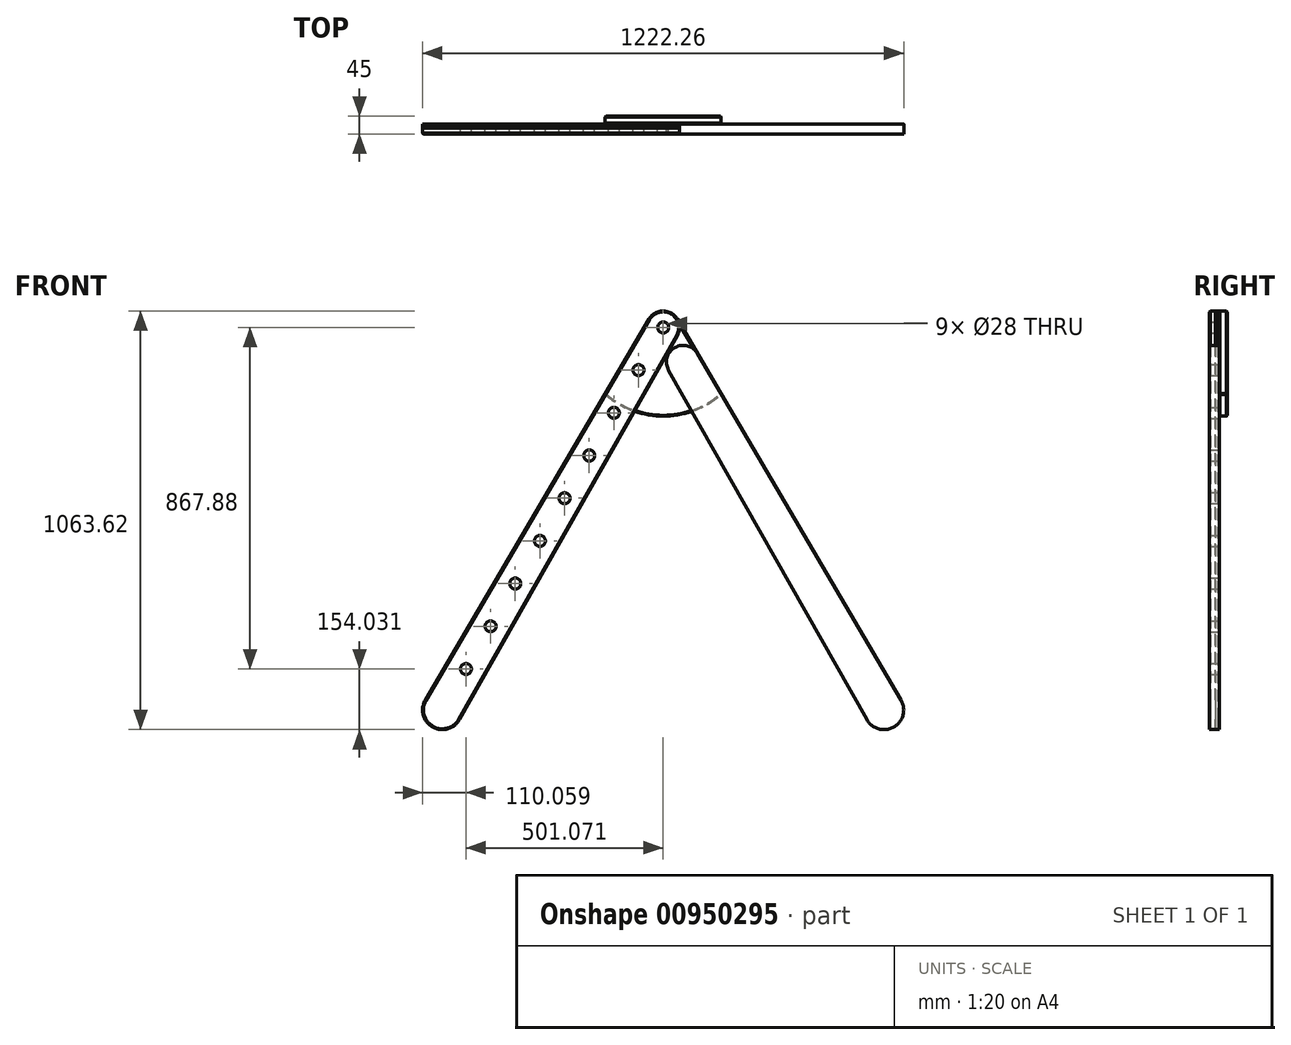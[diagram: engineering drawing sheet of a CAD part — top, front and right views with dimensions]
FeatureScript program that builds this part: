
annotation { "Feature Type Name" : "Feature", "Feature Type Description" : "" }
export const myFeature = defineFeature(function(context is Context, id is Id, definition is map)
    precondition{}
    {
        {
            var Q0;
            Q0=qCreatedBy(makeId("Front.planeOp"),FACE);
            var sketch = newSketch(context, id + "F0", { "sketchPlane" : qUnion([Q0])});
            skLineSegment(sketch, "E0", {"start": v(0, -771.5) * mm, "end": v(-590, -771.5) * mm});
            skLineSegment(sketch, "E1", {"start": v(-590, -771.5) * mm, "end": v(0, 250.4) * mm});
            skLineSegment(sketch, "E2", {"start": v(0, 250.4) * mm, "end": v(0, -771.5) * mm});
            skSolve(sketch);
        }
        {
            var Q0;
            Q0=qCreatedBy(makeId("Front.planeOp"),FACE);
            var sketch = newSketch(context, id + "F1", { "sketchPlane" : qUnion([Q0])});
            skCircle(sketch, "E3", {"center": v(-501.07, -617.48) * mm, "radius": 14 * mm});
            skCircle(sketch, "E4.1.0.0", {"center": v(-438.44, -509) * mm, "radius": 14 * mm});
            skCircle(sketch, "E4.2.0.0", {"center": v(-375.8, -400.5) * mm, "radius": 14 * mm});
            skCircle(sketch, "E4.3.0.0", {"center": v(-313.17, -292.02) * mm, "radius": 14 * mm});
            skCircle(sketch, "E4.4.0.0", {"center": v(-250.54, -183.54) * mm, "radius": 14 * mm});
            skCircle(sketch, "E4.5.0.0", {"center": v(-187.9, -75.05) * mm, "radius": 14 * mm});
            skCircle(sketch, "E4.6.0.0", {"center": v(-125.27, 33.43) * mm, "radius": 14 * mm});
            skCircle(sketch, "E4.7.0.0", {"center": v(-62.63, 141.92) * mm, "radius": 14 * mm});
            skCircle(sketch, "E4.8.0.0", {"center": v(0, 250.4) * mm, "radius": 14 * mm});
            skLineSegment(sketch, "E4.direction1", {"start": v(-501.07, -617.48) * mm, "end": v(-438.44, -509) * mm, "construction": true});
            skSolve(sketch);
        }
        {
            var Q0;
            Q0=qCreatedBy(makeId("Front.planeOp"),FACE);
            var sketch = newSketch(context, id + "F2", { "sketchPlane" : qUnion([Q0])});
            skArc(sketch, "E5", {"start": v(-604.25, -696.19) * mm, "mid": v(-586.13, -764.81) * mm, "end": v(-517.65, -746.19) * mm});
            skLineSegment(sketch, "E6", {"start": v(-604.25, -696.19) * mm, "end": v(-35.97, 271.52) * mm});
            skArc(sketch, "E7", {"start": v(36.28, 229.81) * mm, "mid": v(20.86, 286.53) * mm, "end": v(-35.97, 271.52) * mm});
            skLineSegment(sketch, "E8", {"start": v(36.28, 229.81) * mm, "end": v(-517.65, -746.19) * mm});
            skPoint(sketch, "E9.end.orphan", {"position": v(0, 304.4) * mm});
            skArc(sketch, "E10.MirrorCS", {"start": v(604.25, -696.19) * mm, "mid": v(586.13, -764.81) * mm, "end": v(517.65, -746.19) * mm});
            skLineSegment(sketch, "E11.MirrorCS", {"start": v(604.25, -696.19) * mm, "end": v(35.97, 271.52) * mm});
            skLineSegment(sketch, "E12.MirrorCS", {"start": v(0, 165.9) * mm, "end": v(517.65, -746.19) * mm});
            skLineSegment(sketch, "E13", {"start": v(0, 250.4) * mm, "end": v(561.13, -721.5) * mm});
            skPoint(sketch, "E14.orphan", {"position": v(-36.28, 229.81) * mm});
            skCircle(sketch, "E15", {"center": v(50.78, 162.45) * mm, "radius": 42.46 * mm});
            skSolve(sketch);
        }
        {
            var Q0;
            Q0=qCreatedBy(makeId("Front.planeOp"),FACE);
            var sketch = newSketch(context, id + "F3", { "sketchPlane" : qUnion([Q0])});
            skLineSegment(sketch, "E16.0", {"start": v(604.25, -696.19) * mm, "end": v(87.4, 183.95) * mm});
            skArc(sketch, "E16.1", {"start": v(87.4, 183.95) * mm, "mid": v(29.55, 199.22) * mm, "end": v(13.85, 141.49) * mm});
            skLineSegment(sketch, "E16.2", {"start": v(13.85, 141.49) * mm, "end": v(517.65, -746.19) * mm});
            skArc(sketch, "E16.3", {"start": v(604.25, -696.19) * mm, "mid": v(586.13, -764.81) * mm, "end": v(517.65, -746.19) * mm});
            skPoint(sketch, "E17.orphan", {"position": v(35.97, 271.52) * mm});
            skPoint(sketch, "E18.orphan", {"position": v(0, 165.9) * mm});
            skSolve(sketch);
        }
        {
            var Q0;
            Q0 = qSketchRegion(id + "F3", true);
            extrude(context, id + "F4", {"entities" : qUnion([Q0]), "depth" : 25 * mm, "offsetDistance" : 25 * mm});
        }
        {
            var Q0;
            Q0=qCreatedBy(makeId("Front.planeOp"),FACE);
            var sketch = newSketch(context, id + "F5", { "sketchPlane" : qUnion([Q0])});
            skArc(sketch, "E19.0", {"start": v(-604.25, -696.19) * mm, "mid": v(-586.13, -764.81) * mm, "end": v(-517.65, -746.19) * mm});
            skLineSegment(sketch, "E19.1", {"start": v(-604.25, -696.19) * mm, "end": v(-35.97, 271.52) * mm});
            skArc(sketch, "E19.2", {"start": v(36.28, 229.81) * mm, "mid": v(20.86, 286.53) * mm, "end": v(-35.97, 271.52) * mm});
            skLineSegment(sketch, "E19.3", {"start": v(36.28, 229.81) * mm, "end": v(-517.65, -746.19) * mm});
            skSolve(sketch);
        }
        {
            var Q0;
            Q0 = qSketchRegion(id + "F5", true);
            extrude(context, id + "F6", {"entities" : qUnion([Q0]), "depth" : 25 * mm, "offsetDistance" : 25 * mm});
        }
        {
            var Q0;
            Q0=qCreatedBy(makeId("Front.planeOp"),FACE);
            var sketch = newSketch(context, id + "F7", { "sketchPlane" : qUnion([Q0])});
            skArc(sketch, "E20", {"start": v(-148.1, 80.58) * mm, "mid": v(0, 25.07) * mm, "end": v(148.1, 80.58) * mm});
            skLineSegment(sketch, "E21.0", {"start": v(604.25, -696.19) * mm, "end": v(35.97, 271.52) * mm});
            skLineSegment(sketch, "E21.1", {"start": v(-604.25, -696.19) * mm, "end": v(-35.97, 271.52) * mm});
            skPoint(sketch, "E21.2", {"position": v(-35.97, 271.52) * mm});
            skArc(sketch, "E21.3", {"start": v(35.97, 271.52) * mm, "mid": v(0, 292.11) * mm, "end": v(-35.97, 271.52) * mm});
            skPoint(sketch, "E22.orphan", {"position": v(36.28, 229.81) * mm});
            skSolve(sketch);
        }
        {
            var Q0;
            Q0=makeQuery(id+"F1.imprint","IMPRINT",FACE,{"disambiguationData":[TD([[makeQuery(id+"F1.imprint","IMPRINT",EDGE,{"derivedFrom":sQuery(id+"F1.wireOp",EDGE,"E4.8.0.0")}),1.0]])]});
            var Q1;
            Q1=makeQuery(id+"F1.imprint","IMPRINT",FACE,{"disambiguationData":[TD([[makeQuery(id+"F1.imprint","IMPRINT",EDGE,{"derivedFrom":sQuery(id+"F1.wireOp",EDGE,"E4.7.0.0")}),1.0]])]});
            var Q2;
            Q2=makeQuery(id+"F1.imprint","IMPRINT",FACE,{"disambiguationData":[TD([[makeQuery(id+"F1.imprint","IMPRINT",EDGE,{"derivedFrom":sQuery(id+"F1.wireOp",EDGE,"E4.6.0.0")}),1.0]])]});
            var Q3;
            Q3=makeQuery(id+"F1.imprint","IMPRINT",FACE,{"disambiguationData":[TD([[makeQuery(id+"F1.imprint","IMPRINT",EDGE,{"derivedFrom":sQuery(id+"F1.wireOp",EDGE,"E4.5.0.0")}),1.0]])]});
            var Q4;
            Q4=makeQuery(id+"F1.imprint","IMPRINT",FACE,{"disambiguationData":[TD([[makeQuery(id+"F1.imprint","IMPRINT",EDGE,{"derivedFrom":sQuery(id+"F1.wireOp",EDGE,"E4.4.0.0")}),1.0]])]});
            var Q5;
            Q5=makeQuery(id+"F1.imprint","IMPRINT",FACE,{"disambiguationData":[TD([[makeQuery(id+"F1.imprint","IMPRINT",EDGE,{"derivedFrom":sQuery(id+"F1.wireOp",EDGE,"E4.3.0.0")}),1.0]])]});
            var Q6;
            Q6=makeQuery(id+"F1.imprint","IMPRINT",FACE,{"disambiguationData":[TD([[makeQuery(id+"F1.imprint","IMPRINT",EDGE,{"derivedFrom":sQuery(id+"F1.wireOp",EDGE,"E4.2.0.0")}),1.0]])]});
            var Q7;
            Q7=makeQuery(id+"F1.imprint","IMPRINT",FACE,{"disambiguationData":[TD([[makeQuery(id+"F1.imprint","IMPRINT",EDGE,{"derivedFrom":sQuery(id+"F1.wireOp",EDGE,"E4.1.0.0")}),1.0]])]});
            var Q8;
            Q8=makeQuery(id+"F1.imprint","IMPRINT",FACE,{"disambiguationData":[TD([[makeQuery(id+"F1.imprint","IMPRINT",EDGE,{"derivedFrom":sQuery(id+"F1.wireOp",EDGE,"E3")}),1.0]])]});
            extrude(context, id + "F8", {"entities" : qUnion([Q0, Q1, Q2, Q3, Q4, Q5, Q6, Q7, Q8]), "operationType" : NewBodyOperationType.REMOVE, "depth" : 25 * mm, "offsetDistance" : 25 * mm});
        }
        {
            var Q0;
            Q0 = qSketchRegion(id + "F7", true);
            extrude(context, id + "F9", {"entities" : qUnion([Q0]), "oppositeDirection" : true, "depth" : 20 * mm, "offsetDistance" : 25 * mm});
        }
        {
            var Q0;
            {var subQ5=sQuery(id+"F2.wireOp",EDGE,"E5");Q0=makeQuery(id+"F2.imprint","IMPRINT",FACE,{"disambiguationData":[TD([[makeQuery(id+"F2.imprint","IMPRINT",EDGE,{"derivedFrom":subQ5}),1.0]])]});}
            var Q1;
            Q1=sQuery(id+"F2.wireOp",EDGE,"E5");
            var Q2;
            Q2=sQuery(id+"F2.wireOp",EDGE,"E6");
            var Q3;
            Q3=sQuery(id+"F2.wireOp",EDGE,"E7");
            var Q4;
            Q4=sQuery(id+"F2.wireOp",EDGE,"E8");
            extrude(context, id + "F10", {"entities" : qUnion([Q0]), "surfaceEntities" : qUnion([Q1, Q2, Q3, Q4]), "depth" : 10 * mm, "offsetDistance" : 25 * mm});
        }
        {
            var Q0;
            Q0=makeQuery(id+"F6.opExtrude","CAP_EDGE",EDGE,{"disambiguationData":[OSD([sQuery(id+"F5.wireOp",EDGE,"E19.1")])],"isStart":false});
            var Q1;
            Q1=makeQuery(id+"F6.opExtrude","CAP_EDGE",EDGE,{"disambiguationData":[OSD([sQuery(id+"F5.wireOp",EDGE,"E19.1")])],"isStart":true});
            var Q2;
            Q2=makeQuery(id+"F9.opExtrude","CAP_EDGE",EDGE,{"disambiguationData":[OSD([sQuery(id+"F7.wireOp",EDGE,"E21.3")])],"isStart":false});
            var Q3;
            Q3=makeQuery(id+"F9.opExtrude","SWEPT_EDGE",EDGE,{"disambiguationData":[OSD([sQuery(id+"F7.wireOp",EDGE,"E20"),sQuery(id+"F7.wireOp",EDGE,"E21.1")])]});
            var Q4;
            Q4=makeQuery(id+"F9.opExtrude","CAP_EDGE",EDGE,{"disambiguationData":[OSD([sQuery(id+"F7.wireOp",EDGE,"E20")])],"isStart":false});
            var Q5;
            Q5=makeQuery(id+"F9.opExtrude","CAP_EDGE",EDGE,{"disambiguationData":[OSD([sQuery(id+"F7.wireOp",EDGE,"E21.1")])],"isStart":true});
            var Q6;
            Q6=makeQuery(id+"F9.opExtrude","CAP_EDGE",EDGE,{"disambiguationData":[OSD([sQuery(id+"F7.wireOp",EDGE,"E20")])],"isStart":true});
            var Q7;
            Q7=makeQuery(id+"F9.opExtrude","SWEPT_EDGE",EDGE,{"disambiguationData":[OSD([sQuery(id+"F7.wireOp",EDGE,"E20"),sQuery(id+"F7.wireOp",EDGE,"E21.0")])]});
            chamfer(context, id + "F11", {"entities" : qUnion([Q0, Q1, Q2, Q3, Q4, Q5, Q6, Q7]), "width" : 2 * mm, "tangentPropagation" : true});
        }
    });
